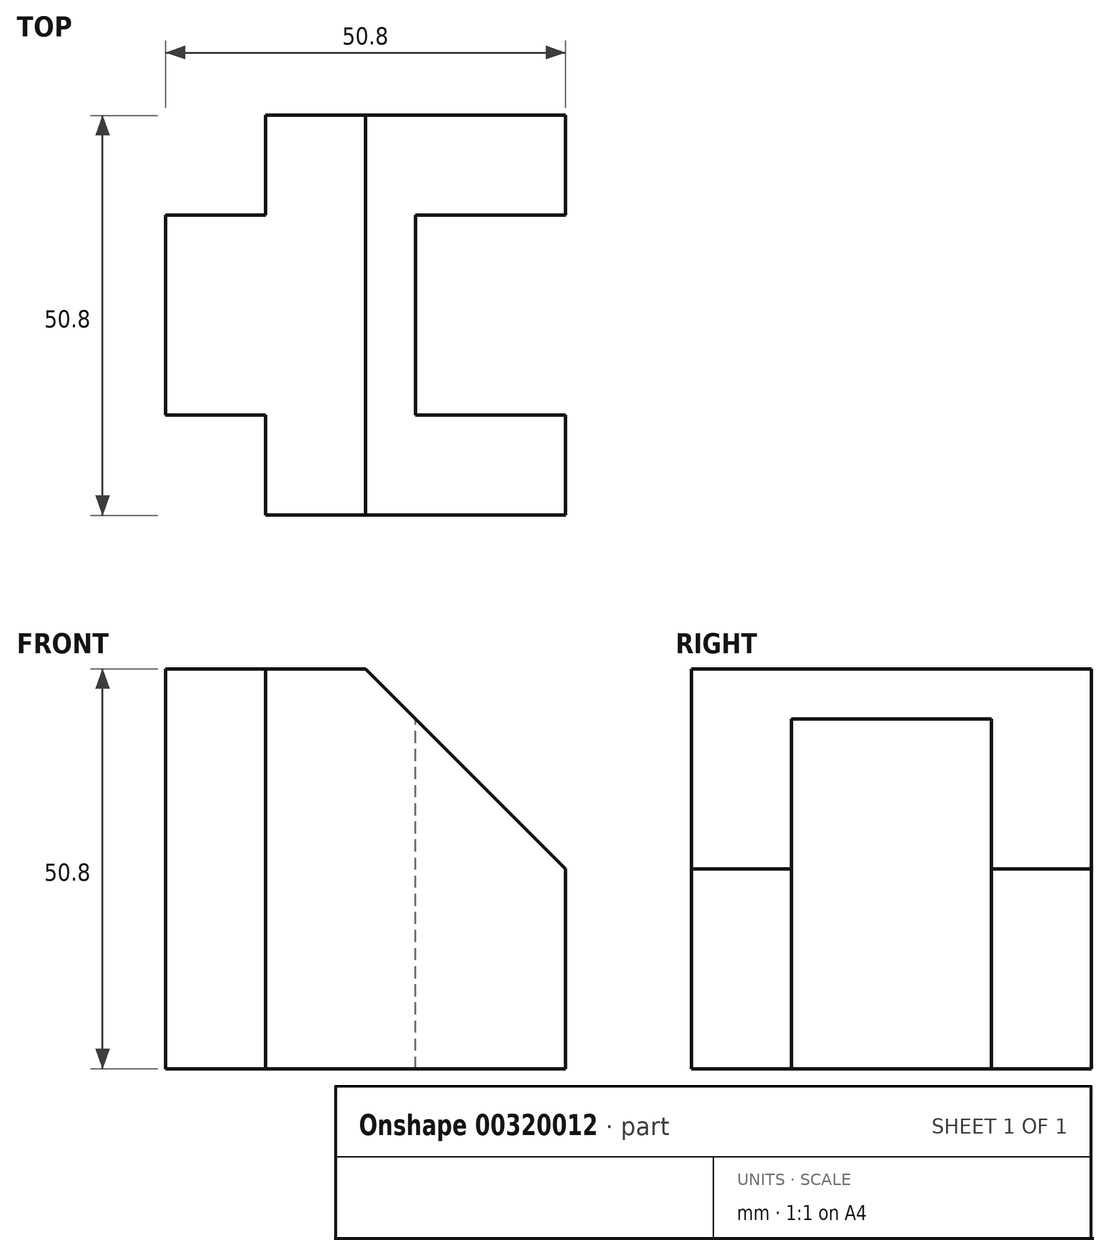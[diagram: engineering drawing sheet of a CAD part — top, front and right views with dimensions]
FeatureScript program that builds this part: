
annotation { "Feature Type Name" : "Feature", "Feature Type Description" : "" }
export const myFeature = defineFeature(function(context is Context, id is Id, definition is map)
    precondition{}
    {
        {
            var Q0;
            Q0=qCreatedBy(makeId("Top.planeOp"),FACE);
            var sketch = newSketch(context, id + "F0", { "sketchPlane" : qUnion([Q0])});
            skLineSegment(sketch, "E0", {"start": v(-29.3, 21.18) * mm, "end": v(-16.6, 21.18) * mm});
            skLineSegment(sketch, "E1", {"start": v(-16.6, 21.18) * mm, "end": v(-16.6, 33.88) * mm});
            skLineSegment(sketch, "E2", {"start": v(-16.6, 33.88) * mm, "end": v(21.5, 33.88) * mm});
            skLineSegment(sketch, "E3", {"start": v(21.5, 33.88) * mm, "end": v(21.5, -16.92) * mm});
            skLineSegment(sketch, "E4", {"start": v(21.5, -16.92) * mm, "end": v(-16.6, -16.92) * mm});
            skLineSegment(sketch, "E5", {"start": v(-16.6, -16.92) * mm, "end": v(-16.6, -4.22) * mm});
            skLineSegment(sketch, "E6", {"start": v(-16.6, -4.22) * mm, "end": v(-29.3, -4.22) * mm});
            skLineSegment(sketch, "E7", {"start": v(-29.3, -4.22) * mm, "end": v(-29.3, 21.18) * mm});
            skSolve(sketch);
        }
        {
            var Q0;
            Q0 = qSketchRegion(id + "F0", true);
            extrude(context, id + "F1", {"entities" : qUnion([Q0]), "oppositeDirection" : true, "depth" : 50.8 * mm});
        }
        {
            var Q0;
            Q0=makeQuery(id+"F1.opExtrude","CAP_FACE",FACE,{"disambiguationData":[OSD([sQuery(id+"F0.wireOp",EDGE,"E0"),sQuery(id+"F0.wireOp",EDGE,"E1"),sQuery(id+"F0.wireOp",EDGE,"E2"),sQuery(id+"F0.wireOp",EDGE,"E3"),sQuery(id+"F0.wireOp",EDGE,"E4"),sQuery(id+"F0.wireOp",EDGE,"E5"),sQuery(id+"F0.wireOp",EDGE,"E6"),sQuery(id+"F0.wireOp",EDGE,"E7")])],"isStart":true});
            var sketch = newSketch(context, id + "F2", { "sketchPlane" : qUnion([Q0])});
            skLineSegment(sketch, "E8", {"start": v(21.5, 8.48) * mm, "end": v(21.5, 21.18) * mm});
            skLineSegment(sketch, "E9", {"start": v(21.5, 21.18) * mm, "end": v(2.45, 21.18) * mm});
            skLineSegment(sketch, "E10", {"start": v(2.45, 21.18) * mm, "end": v(2.45, -4.22) * mm});
            skLineSegment(sketch, "E11", {"start": v(2.45, -4.22) * mm, "end": v(21.5, -4.22) * mm});
            skLineSegment(sketch, "E12", {"start": v(21.5, -4.22) * mm, "end": v(21.5, 8.48) * mm});
            skSolve(sketch);
        }
        {
            var Q0;
            Q0 = qSketchRegion(id + "F2", true);
            extrude(context, id + "F3", {"entities" : qUnion([Q0]), "operationType" : NewBodyOperationType.REMOVE, "oppositeDirection" : true, "depth" : 50.8 * mm});
        }
        {
            var Q0;
            Q0=makeQuery(id+"F1.opExtrude","SWEPT_FACE",FACE,{"disambiguationData":[OSD([sQuery(id+"F0.wireOp",EDGE,"E4")])]});
            var sketch = newSketch(context, id + "F4", { "sketchPlane" : qUnion([Q0])});
            skLineSegment(sketch, "E13", {"start": v(21.5, -25.4) * mm, "end": v(21.5, 0) * mm});
            skLineSegment(sketch, "E14", {"start": v(21.5, 0) * mm, "end": v(-3.9, 0) * mm});
            skLineSegment(sketch, "E15", {"start": v(-3.9, 0) * mm, "end": v(21.5, -25.4) * mm});
            skSolve(sketch);
        }
        {
            var Q0;
            Q0 = qSketchRegion(id + "F4", true);
            extrude(context, id + "F5", {"entities" : qUnion([Q0]), "operationType" : NewBodyOperationType.REMOVE, "oppositeDirection" : true, "depth" : 50.8 * mm});
        }
    });
